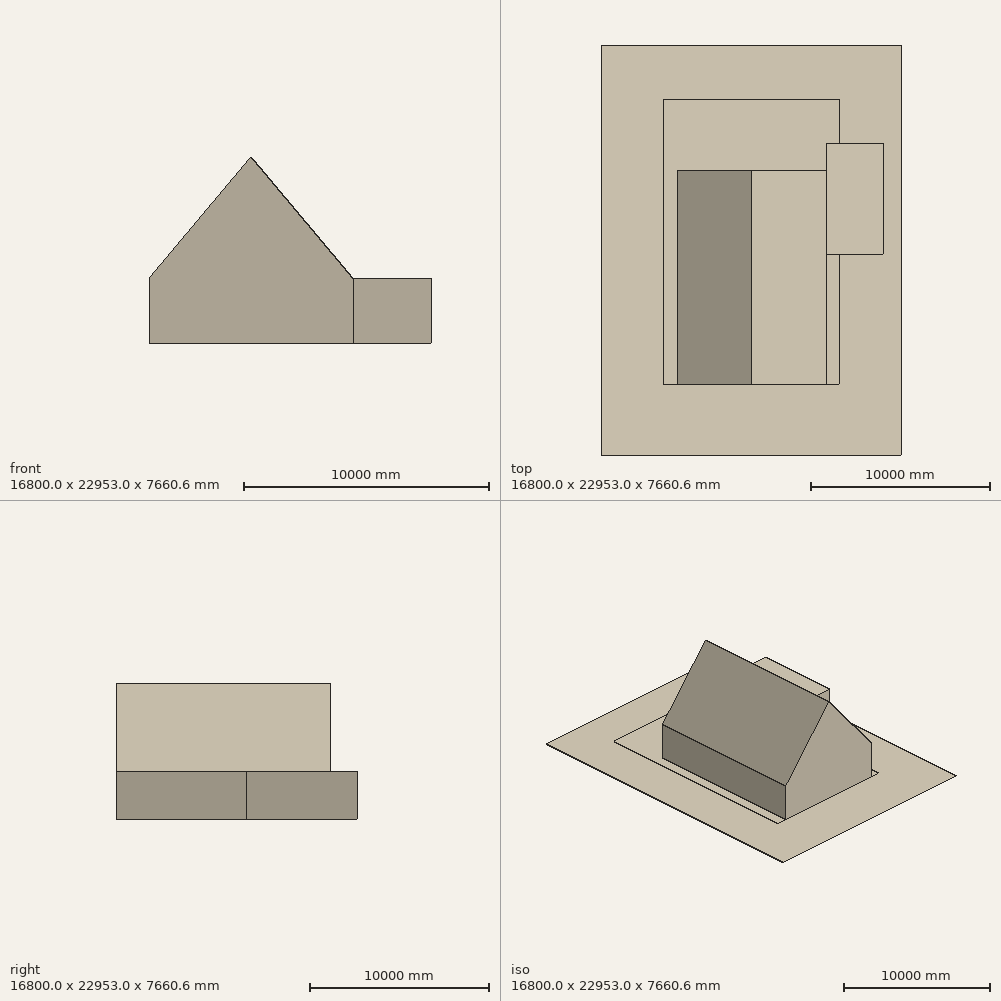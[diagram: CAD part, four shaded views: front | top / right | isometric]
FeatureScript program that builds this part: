
annotation { "Feature Type Name" : "Feature", "Feature Type Description" : "" }
export const myFeature = defineFeature(function(context is Context, id is Id, definition is map)
    precondition{}
    {
        {
            var Q0;
            Q0=qCreatedBy(makeId("Top.planeOp"),FACE);
            var sketch = newSketch(context, id + "F0", { "sketchPlane" : qUnion([Q0])});
            skLineSegment(sketch, "E0.bottom", {"start": v(-5071.58, -11461.11) * mm, "end": v(11728.42, -11461.11) * mm});
            skLineSegment(sketch, "E0.top", {"start": v(-5071.58, 11491.89) * mm, "end": v(11728.42, 11491.89) * mm});
            skLineSegment(sketch, "E0.left", {"start": v(-5071.58, -11461.11) * mm, "end": v(-5071.58, 11491.89) * mm});
            skLineSegment(sketch, "E0.right", {"start": v(11728.42, -11461.11) * mm, "end": v(11728.42, 11491.89) * mm});
            skSolve(sketch);
        }
        {
            var Q0;
            Q0=makeQuery(id+"F0.imprint","IMPRINT",FACE,{"disambiguationData":[TD([[makeQuery(id+"F0.imprint","IMPRINT",EDGE,{"derivedFrom":sQuery(id+"F0.wireOp",EDGE,"E0.bottom")}),1.0]])]});
            extrude(context, id + "F1", {"entities" : qUnion([Q0]), "depth" : 25 * mm, "offsetDistance" : 25 * mm});
        }
        {
            var Q0;
            Q0=makeQuery(id+"F1.opExtrude","CAP_FACE",FACE,{"disambiguationData":[OSD([sQuery(id+"F0.wireOp",EDGE,"E0.bottom"),sQuery(id+"F0.wireOp",EDGE,"E0.top"),sQuery(id+"F0.wireOp",EDGE,"E0.left"),sQuery(id+"F0.wireOp",EDGE,"E0.right")])],"isStart":false});
            var sketch = newSketch(context, id + "F2", { "sketchPlane" : qUnion([Q0])});
            skLineSegment(sketch, "E1.bottom", {"start": v(-1571.58, 8491.89) * mm, "end": v(8228.42, 8491.89) * mm});
            skLineSegment(sketch, "E1.top", {"start": v(-1571.58, -7461.11) * mm, "end": v(8228.42, -7461.11) * mm});
            skLineSegment(sketch, "E1.left", {"start": v(-1571.58, 8491.89) * mm, "end": v(-1571.58, -7461.11) * mm});
            skLineSegment(sketch, "E1.right", {"start": v(8228.42, 8491.89) * mm, "end": v(8228.42, -7461.11) * mm});
            skSolve(sketch);
        }
        {
            var Q0;
            Q0=qSketchRegion(id+"F2",true);
            extrude(context, id + "F3", {"entities" : qUnion([Q0]), "operationType" : NewBodyOperationType.ADD, "depth" : 10 * mm, "offsetDistance" : 25 * mm});
        }
        {
            var Q0;
            Q0=makeQuery(id+"F1.opExtrude","CAP_FACE",FACE,{"disambiguationData":[OSD([sQuery(id+"F0.wireOp",EDGE,"E0.bottom"),sQuery(id+"F0.wireOp",EDGE,"E0.top"),sQuery(id+"F0.wireOp",EDGE,"E0.left"),sQuery(id+"F0.wireOp",EDGE,"E0.right")])],"isStart":false});
            var sketch = newSketch(context, id + "F4", { "sketchPlane" : qUnion([Q0])});
            skLineSegment(sketch, "E2.bottom", {"start": v(-1571.58, 8491.89) * mm, "end": v(-4071.58, 8491.89) * mm});
            skLineSegment(sketch, "E2.top", {"start": v(-1571.58, -6461.11) * mm, "end": v(-4071.58, -6461.11) * mm});
            skLineSegment(sketch, "E2.left", {"start": v(-1571.58, 8491.89) * mm, "end": v(-1571.58, -6461.11) * mm});
            skLineSegment(sketch, "E2.right", {"start": v(-4071.58, 8491.89) * mm, "end": v(-4071.58, -6461.11) * mm});
            skLineSegment(sketch, "E3.bottom", {"start": v(8228.42, 8491.89) * mm, "end": v(10728.42, 8491.89) * mm});
            skLineSegment(sketch, "E3.top", {"start": v(8228.42, -4461.11) * mm, "end": v(10728.42, -4461.11) * mm});
            skLineSegment(sketch, "E3.left", {"start": v(8228.42, 8491.89) * mm, "end": v(8228.42, -4461.11) * mm});
            skLineSegment(sketch, "E3.right", {"start": v(10728.42, 8491.89) * mm, "end": v(10728.42, -4461.11) * mm});
            skSolve(sketch);
        }
        {
            var Q0;
            Q0=makeQuery(id+"F3.opExtrude","CAP_FACE",FACE,{"disambiguationData":[OSD([sQuery(id+"F2.wireOp",EDGE,"E1.bottom"),sQuery(id+"F2.wireOp",EDGE,"E1.top"),sQuery(id+"F2.wireOp",EDGE,"E1.left"),sQuery(id+"F2.wireOp",EDGE,"E1.right")])],"isStart":false});
            var sketch = newSketch(context, id + "F5", { "sketchPlane" : qUnion([Q0])});
            skLineSegment(sketch, "E4.bottom", {"start": v(7528.42, -7461.11) * mm, "end": v(-821.58, -7461.11) * mm});
            skLineSegment(sketch, "E4.top", {"start": v(7528.42, 4488.89) * mm, "end": v(-821.58, 4488.89) * mm});
            skLineSegment(sketch, "E4.left", {"start": v(7528.42, -7461.11) * mm, "end": v(7528.42, -186.11) * mm});
            skLineSegment(sketch, "E4.right", {"start": v(-821.58, -7461.11) * mm, "end": v(-821.58, 4488.89) * mm});
            skLineSegment(sketch, "E5.bottom", {"start": v(7528.42, -186.11) * mm, "end": v(10728.42, -186.11) * mm});
            skLineSegment(sketch, "E5.top", {"start": v(7528.42, 6013.89) * mm, "end": v(10728.42, 6013.89) * mm});
            skLineSegment(sketch, "E5.left", {"start": v(7528.42, 4488.89) * mm, "end": v(7528.42, 6013.89) * mm});
            skLineSegment(sketch, "E5.right", {"start": v(10728.42, -186.11) * mm, "end": v(10728.42, 6013.89) * mm});
            skLineSegment(sketch, "E6", {"start": v(-821.58, -1486.11) * mm, "end": v(7528.42, -1486.11) * mm, "construction": true});
            skLineSegment(sketch, "E7", {"start": v(7528.42, -686.11) * mm, "end": v(-821.58, -686.11) * mm});
            skSolve(sketch);
        }
        {
            var Q0;
            Q0=qSketchRegion(id+"F5",true);
            extrude(context, id + "F6", {"entities" : qUnion([Q0]), "operationType" : NewBodyOperationType.ADD, "depth" : 2650 * mm, "offsetDistance" : 25 * mm});
        }
        {
            var Q0;
            Q0=makeQuery(id+"F6.boolean.opBoolean","MERGE",FACE,{"derivedFrom":[makeQuery(id+"F3.opExtrude","SWEPT_FACE",FACE,{"disambiguationData":[OSD([sQuery(id+"F2.wireOp",EDGE,"E1.top")])]}),makeQuery(id+"F6.opExtrude","SWEPT_FACE",FACE,{"disambiguationData":[OSD([sQuery(id+"F5.wireOp",EDGE,"E4.bottom")])]})]});
            var sketch = newSketch(context, id + "F7", { "sketchPlane" : qUnion([Q0])});
            skLineSegment(sketch, "E8", {"start": v(-821.58, 2685) * mm, "end": v(3353.42, 7660.57) * mm});
            skLineSegment(sketch, "E9", {"start": v(3353.42, 7660.57) * mm, "end": v(7528.42, 2685) * mm});
            skLineSegment(sketch, "E10", {"start": v(7528.42, 2685) * mm, "end": v(-821.58, 2685) * mm});
            skSolve(sketch);
        }
        {
            var Q0;
            Q0=qSketchRegion(id+"F7",true);
            var Q1;
            Q1=makeQuery(id+"F6.opExtrude","SWEPT_FACE",FACE,{"disambiguationData":[OSD([sQuery(id+"F5.wireOp",EDGE,"E4.top")])]});
            extrude(context, id + "F8", {"entities" : qUnion([Q0]), "operationType" : NewBodyOperationType.ADD, "endBound" : BoundingType.UP_TO_SURFACE, "oppositeDirection" : true, "depth" : 6260 * mm, "endBoundEntityFace" : qUnion([Q1]), "offsetDistance" : 25 * mm});
        }
    });
